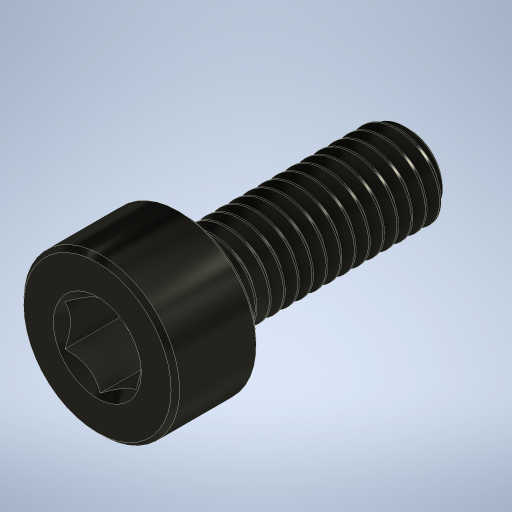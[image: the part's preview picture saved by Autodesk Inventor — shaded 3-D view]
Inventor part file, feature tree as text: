
AUTODESK INVENTOR PART (.ipt)
format: ipt  version: 2024 (Build 280153000, 153)  size: 614,400 bytes
history: native  units: in
note: dims shown in document units (in); Inventor stores cm internally (conversion verified against a paired STEP export)
features: revolve x1
ambient origin geometry x8: Origin, YZ Plane, XZ Plane, XY Plane, X Axis, Y Axis, Z Axis, Center Point
bodies: Solid1 (feature_tree)
feature tree (1):
  revolve  "Revolve2"  [1 undecoded]
note: 1 required parameter value undecoded (feature->parameter linkage not recoverable at this tier; creation-order binding heuristic only, values carry confidence <= 0.55)
